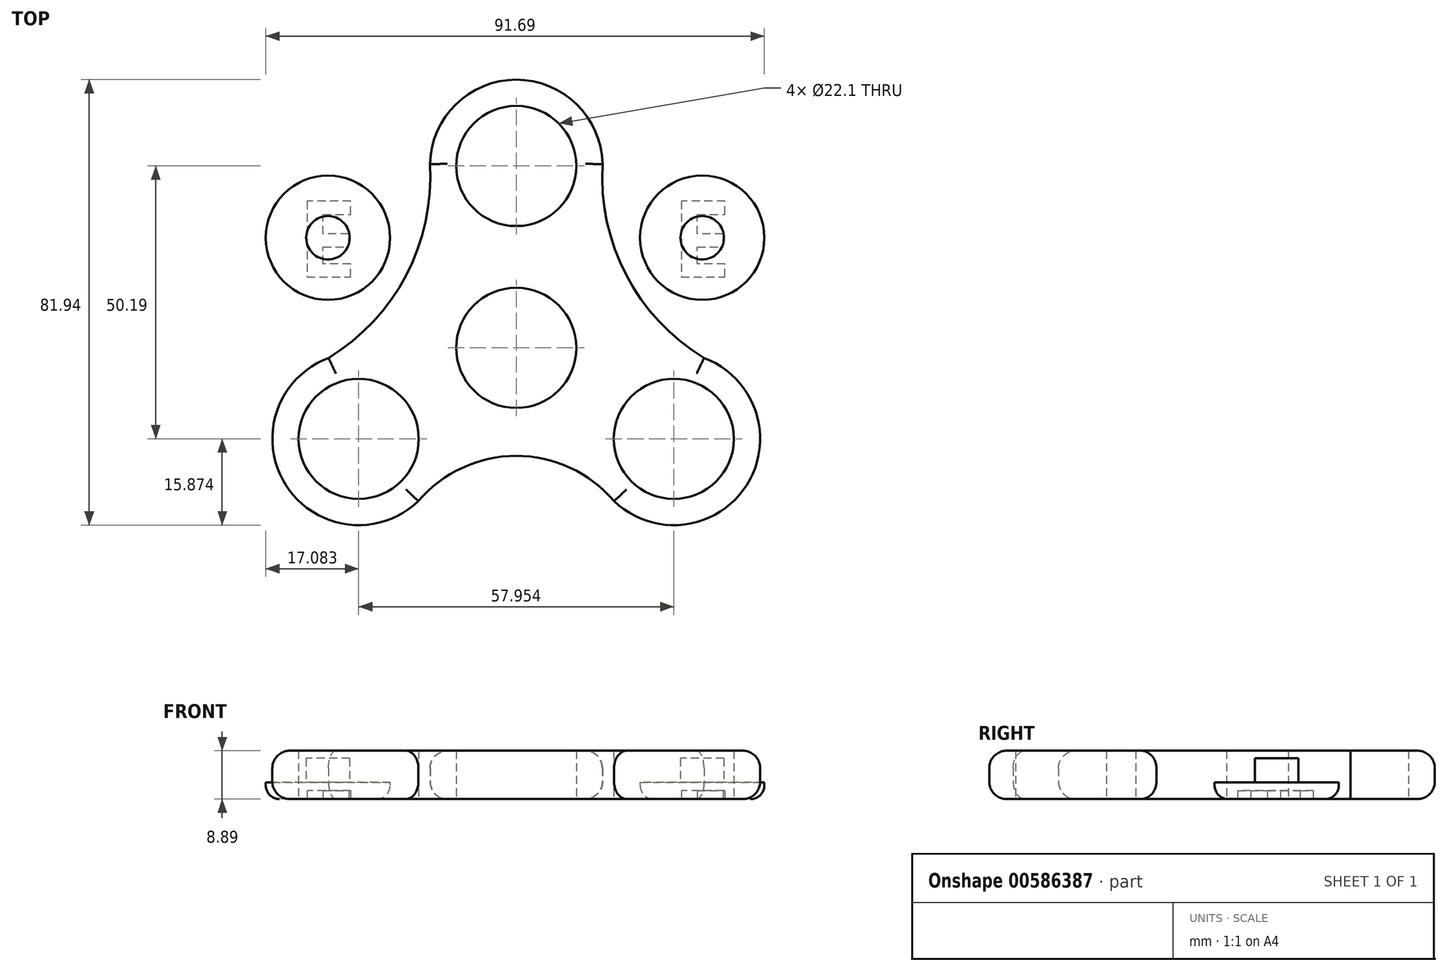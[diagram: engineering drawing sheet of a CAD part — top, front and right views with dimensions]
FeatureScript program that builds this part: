
annotation { "Feature Type Name" : "Feature", "Feature Type Description" : "" }
export const myFeature = defineFeature(function(context is Context, id is Id, definition is map)
    precondition{}
    {
        {
            var Q0;
            Q0=qCreatedBy(makeId("Top.planeOp"),FACE);
            var sketch = newSketch(context, id + "F0", { "sketchPlane" : qUnion([Q0])});
            skCircle(sketch, "E0", {"center": v(0, 61.65) * mm, "radius": 11.05 * mm});
            skCircle(sketch, "E1.1.0", {"center": v(-28.98, 11.46) * mm, "radius": 11.05 * mm});
            skCircle(sketch, "E1.2.0", {"center": v(28.98, 11.46) * mm, "radius": 11.05 * mm});
            skPoint(sketch, "E1.center", {"position": v(0, 28.2) * mm});
            skCircle(sketch, "E2", {"center": v(0, 28.2) * mm, "radius": 11.05 * mm});
            skArc(sketch, "E3", {"start": v(15.8, 60.14) * mm, "mid": v(0, 77.53) * mm, "end": v(-15.8, 60.14) * mm});
            skArc(sketch, "E4", {"start": v(-34.54, 26.33) * mm, "mid": v(-41.87, 2.2) * mm, "end": v(-16.66, 1.45) * mm});
            skArc(sketch, "E5", {"start": v(16.66, 1.45) * mm, "mid": v(41.87, 2.2) * mm, "end": v(34.54, 26.33) * mm});
            skArc(sketch, "E6", {"start": v(-34.54, 26.33) * mm, "mid": v(-20.24, 41.57) * mm, "end": v(-15.87, 62) * mm});
            skArc(sketch, "E7.MirrorCS", {"start": v(34.54, 26.33) * mm, "mid": v(20.24, 41.57) * mm, "end": v(15.87, 62) * mm});
            skArc(sketch, "E8", {"start": v(18, 0) * mm, "mid": v(0, 8.34) * mm, "end": v(-18, 0) * mm});
            skSolve(sketch);
        }
        {
            var Q0;
            Q0=makeQuery(id+"F0.imprint","IMPRINT",FACE,{"disambiguationData":[TD([[makeQuery(id+"F0.imprint","IMPRINT",EDGE,{"derivedFrom":sQuery(id+"F0.wireOp",EDGE,"E0")}),-1.0]])]});
            extrude(context, id + "F1", {"entities" : qUnion([Q0]), "depth" : 8.9 * mm, "offsetDistance" : 25.4 * mm});
        }
        {
            var Q0;
            Q0=makeQuery(id+"F1.opExtrude","CAP_EDGE",EDGE,{"disambiguationData":[OSD([sQuery(id+"F0.wireOp",EDGE,"E4")])],"isStart":false});
            var Q1;
            Q1=makeQuery(id+"F1.opExtrude","CAP_EDGE",EDGE,{"disambiguationData":[OSD([sQuery(id+"F0.wireOp",EDGE,"E8")])],"isStart":false});
            var Q2;
            Q2=makeQuery(id+"F1.opExtrude","CAP_EDGE",EDGE,{"disambiguationData":[OSD([sQuery(id+"F0.wireOp",EDGE,"E7.MirrorCS")])],"isStart":false});
            var Q3;
            Q3=makeQuery(id+"F1.opExtrude","CAP_EDGE",EDGE,{"disambiguationData":[OSD([sQuery(id+"F0.wireOp",EDGE,"E3")])],"isStart":false});
            var Q4;
            Q4=makeQuery(id+"F1.opExtrude","CAP_EDGE",EDGE,{"disambiguationData":[OSD([sQuery(id+"F0.wireOp",EDGE,"E6")])],"isStart":false});
            var Q5;
            Q5=makeQuery(id+"F1.opExtrude","CAP_EDGE",EDGE,{"disambiguationData":[OSD([sQuery(id+"F0.wireOp",EDGE,"E5")])],"isStart":false});
            var Q6;
            Q6=makeQuery(id+"F1.opExtrude","CAP_EDGE",EDGE,{"disambiguationData":[OSD([sQuery(id+"F0.wireOp",EDGE,"E4")])],"isStart":true});
            var Q7;
            Q7=makeQuery(id+"F1.opExtrude","CAP_EDGE",EDGE,{"disambiguationData":[OSD([sQuery(id+"F0.wireOp",EDGE,"E8")])],"isStart":true});
            var Q8;
            Q8=makeQuery(id+"F1.opExtrude","CAP_EDGE",EDGE,{"disambiguationData":[OSD([sQuery(id+"F0.wireOp",EDGE,"E5")])],"isStart":true});
            var Q9;
            Q9=makeQuery(id+"F1.opExtrude","CAP_EDGE",EDGE,{"disambiguationData":[OSD([sQuery(id+"F0.wireOp",EDGE,"E7.MirrorCS")])],"isStart":true});
            var Q10;
            Q10=makeQuery(id+"F1.opExtrude","CAP_EDGE",EDGE,{"disambiguationData":[OSD([sQuery(id+"F0.wireOp",EDGE,"E3")])],"isStart":true});
            var Q11;
            Q11=makeQuery(id+"F1.opExtrude","CAP_EDGE",EDGE,{"disambiguationData":[OSD([sQuery(id+"F0.wireOp",EDGE,"E6")])],"isStart":true});
            fillet(context, id + "F2", {"entities" : qUnion([Q0, Q1, Q2, Q3, Q4, Q5, Q6, Q7, Q8, Q9, Q10, Q11]), "radius" : 3.17 * mm, "tangentPropagation" : true, "allowEdgeOverflow" : false});
        }
        {
            var Q0;
            Q0=qCreatedBy(makeId("Top.planeOp"),FACE);
            var sketch = newSketch(context, id + "F3", { "sketchPlane" : qUnion([Q0])});
            skCircle(sketch, "E9", {"center": v(34.2, 48.46) * mm, "radius": 11.43 * mm});
            skSolve(sketch);
        }
        {
            var Q0;
            Q0=makeQuery(id+"F3.imprint","IMPRINT",FACE,{"disambiguationData":[TD([[makeQuery(id+"F3.imprint","IMPRINT",EDGE,{"derivedFrom":sQuery(id+"F3.wireOp",EDGE,"E9")}),1.0]])]});
            extrude(context, id + "F4", {"entities" : qUnion([Q0]), "depth" : 3.05 * mm, "offsetDistance" : 25.4 * mm});
        }
        {
            var Q0;
            Q0=makeQuery(id+"F4.opExtrude","CAP_FACE",FACE,{"disambiguationData":[OSD([sQuery(id+"F3.wireOp",EDGE,"E9")])],"isStart":false});
            var sketch = newSketch(context, id + "F5", { "sketchPlane" : qUnion([Q0])});
            skCircle(sketch, "E10", {"center": v(34.2, 48.46) * mm, "radius": 4 * mm});
            skSolve(sketch);
        }
        {
            var Q0;
            Q0=makeQuery(id+"F5.imprint","IMPRINT",FACE,{"disambiguationData":[TD([[makeQuery(id+"F5.imprint","IMPRINT",EDGE,{"derivedFrom":sQuery(id+"F5.wireOp",EDGE,"E10")}),1.0]])]});
            extrude(context, id + "F6", {"entities" : qUnion([Q0]), "operationType" : NewBodyOperationType.ADD, "depth" : 4.44 * mm, "offsetDistance" : 25.4 * mm});
        }
        {
            var Q0;
            Q0=makeQuery(id+"F4.opExtrude","CAP_EDGE",EDGE,{"disambiguationData":[OSD([sQuery(id+"F3.wireOp",EDGE,"E9")])],"isStart":true});
            fillet(context, id + "F7", {"entities" : qUnion([Q0]), "radius" : 2.54 * mm, "tangentPropagation" : true, "allowEdgeOverflow" : false});
        }
        {
            var Q0;
            Q0=makeQuery(id+"F4.opExtrude","CAP_FACE",FACE,{"disambiguationData":[OSD([sQuery(id+"F3.wireOp",EDGE,"E9")])],"isStart":true});
            var sketch = newSketch(context, id + "F8", { "sketchPlane" : qUnion([Q0])});
            skText(sketch, "E11", { "text": "E", "fontName": "OpenSans-Bold.ttf"});
            const initialGuessF8  = {"E11": [0.02859, -0.0552, 1, 0, 0.01407]};
            skSetInitialGuess(sketch, initialGuessF8);
            skSolve(sketch);
        }
        {
            var Q0;
            Q0=makeQuery(id+"F8.imprint","IMPRINT",FACE,{"disambiguationData":[TD([[makeQuery(id+"F8.imprint","IMPRINT",EDGE,{"derivedFrom":sQuery(id+"F8.wireOp",EDGE,"E11.sketch_text.stroke-0")}),-1.0]])]});
            extrude(context, id + "F9", {"entities" : qUnion([Q0]), "operationType" : NewBodyOperationType.REMOVE, "oppositeDirection" : true, "depth" : 1.52 * mm, "offsetDistance" : 25.4 * mm});
        }
        {
            var Q0;
            Q0=makeQuery(id+"F4.opExtrude","SWEPT_BODY",BODY,{"disambiguationData":[OSD([sQuery(id+"F3.wireOp",EDGE,"E9")])]});
            transform(context, id + "F10", {"entities" : qUnion([Q0]), "transformType" : TransformType.TRANSLATION_3D, "dx" : -68.83 * mm, "dy" : 0 * mm, "dz" : 0 * mm, "makeCopy" : true});
        }
    });
